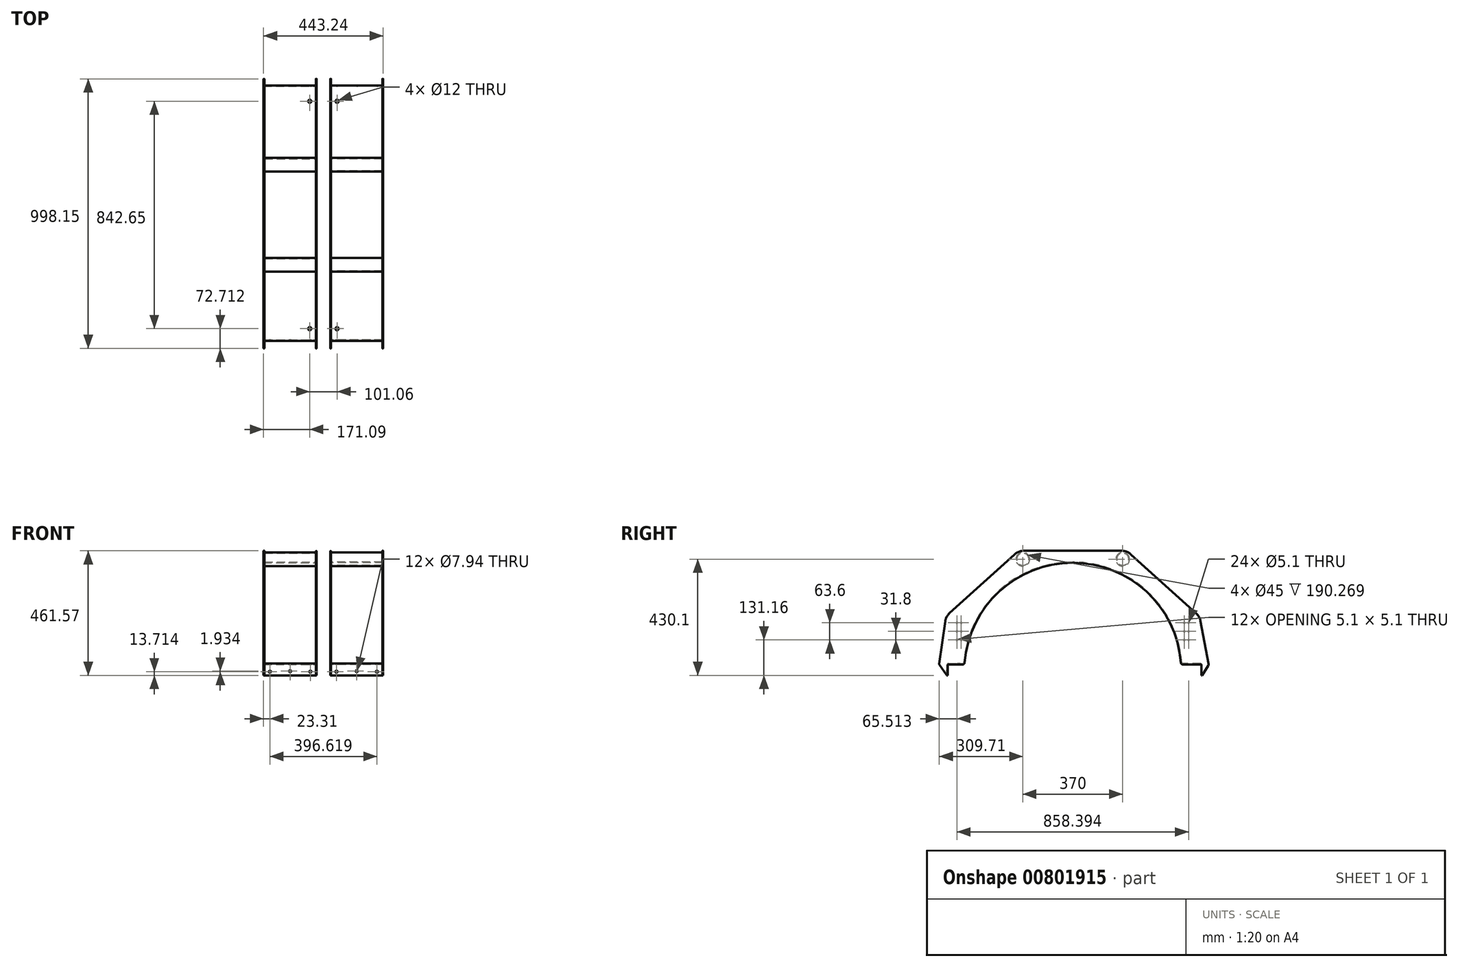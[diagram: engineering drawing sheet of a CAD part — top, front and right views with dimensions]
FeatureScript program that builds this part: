
annotation { "Feature Type Name" : "Feature", "Feature Type Description" : "" }
export const myFeature = defineFeature(function(context is Context, id is Id, definition is map)
    precondition{}
    {
        {
            var Q0;
            Q0=qCreatedBy(makeId("Right.planeOp"),FACE);
            var sketch = newSketch(context, id + "F0", { "sketchPlane" : qUnion([Q0])});
            skArc(sketch, "E0", {"start": v(-400.78, 31.26) * mm, "mid": v(0, 402) * mm, "end": v(400.78, 31.26) * mm});
            skLineSegment(sketch, "E1", {"start": v(-456.53, 215.37) * mm, "end": v(-216.59, 432.1) * mm});
            skLineSegment(sketch, "E2", {"start": v(457.5, 214.5) * mm, "end": v(216.59, 432.1) * mm});
            skLineSegment(sketch, "E3", {"start": v(183.07, 445) * mm, "end": v(-183.07, 445) * mm});
            skLineSegment(sketch, "E4", {"start": v(407.11, 25.4) * mm, "end": v(473.02, 25.4) * mm});
            skLineSegment(sketch, "E5", {"start": v(-460.32, 25.4) * mm, "end": v(-407.11, 25.4) * mm});
            skPoint(sketch, "E6.visualSharp", {"position": v(202.3, 445) * mm});
            skPoint(sketch, "E7.visualSharp", {"position": v(-401.2, 25.4) * mm});
            skArc(sketch, "E7.filletArc", {"start": v(-407.11, 25.4) * mm, "mid": v(-402.8, 27.09) * mm, "end": v(-400.78, 31.26) * mm});
            skPoint(sketch, "E8.visualSharp", {"position": v(401.2, 25.4) * mm});
            skArc(sketch, "E8.filletArc", {"start": v(400.78, 31.26) * mm, "mid": v(402.8, 27.09) * mm, "end": v(407.11, 25.4) * mm});
            skPoint(sketch, "E9.endSnap0", {"position": v(0, 402) * mm});
            skPoint(sketch, "E10", {"position": v(0, 445) * mm});
            skLineSegment(sketch, "E11", {"start": v(-472.53, 185.23) * mm, "end": v(-494.65, 27.9) * mm});
            skLineSegment(sketch, "E12", {"start": v(-493.54, 23.34) * mm, "end": v(-466.3, -15.1) * mm});
            skLineSegment(sketch, "E13", {"start": v(-463.5, -15.1) * mm, "end": v(-463.5, 22.22) * mm});
            skPoint(sketch, "E14.visualSharp", {"position": v(-470, 203.2) * mm});
            skArc(sketch, "E14.filletArc", {"start": v(-456.53, 215.37) * mm, "mid": v(-467.18, 201.7) * mm, "end": v(-472.53, 185.23) * mm});
            skPoint(sketch, "E15.visualSharp", {"position": v(-495, 25.4) * mm});
            skArc(sketch, "E15.filletArc", {"start": v(-494.65, 27.9) * mm, "mid": v(-494.53, 25.51) * mm, "end": v(-493.54, 23.34) * mm});
            skPoint(sketch, "E16.visualSharp", {"position": v(-463.5, 25.4) * mm});
            skArc(sketch, "E16.filletArc", {"start": v(-460.32, 25.4) * mm, "mid": v(-462.57, 24.47) * mm, "end": v(-463.5, 22.22) * mm});
            skLineSegment(sketch, "E17", {"start": v(476.2, 22.22) * mm, "end": v(476.2, -15.1) * mm});
            skPoint(sketch, "E18", {"position": v(505, 25.4) * mm});
            skLineSegment(sketch, "E19", {"start": v(479.37, -15.1) * mm, "end": v(502.46, 21.38) * mm});
            skLineSegment(sketch, "E20", {"start": v(503.33, 25.95) * mm, "end": v(473.12, 186.63) * mm});
            skPoint(sketch, "E21.visualSharp", {"position": v(470, 203.2) * mm});
            skArc(sketch, "E21.filletArc", {"start": v(473.12, 186.63) * mm, "mid": v(467.59, 201.85) * mm, "end": v(457.5, 214.5) * mm});
            skArc(sketch, "E22.filletArc", {"start": v(502.46, 21.38) * mm, "mid": v(503.33, 23.59) * mm, "end": v(503.33, 25.95) * mm});
            skLineSegment(sketch, "E23", {"start": v(476.2, -15.1) * mm, "end": v(479.37, -15.1) * mm});
            skLineSegment(sketch, "E24", {"start": v(-466.3, -15.1) * mm, "end": v(-463.5, -15.1) * mm});
            skPoint(sketch, "E25.visualSharp", {"position": v(476.2, 25.4) * mm});
            skArc(sketch, "E25.filletArc", {"start": v(476.2, 22.22) * mm, "mid": v(475.27, 24.47) * mm, "end": v(473.02, 25.4) * mm});
            skPoint(sketch, "E26", {"position": v(-429.2, 116.06) * mm});
            skPoint(sketch, "E27", {"position": v(-413.2, 116.06) * mm});
            skPoint(sketch, "E28", {"position": v(-413.2, 147.86) * mm});
            skPoint(sketch, "E29", {"position": v(-429.2, 147.86) * mm});
            skPoint(sketch, "E30", {"position": v(-429.2, 179.66) * mm});
            skPoint(sketch, "E31", {"position": v(-413.2, 179.66) * mm});
            skPoint(sketch, "E32", {"position": v(413.2, 179.66) * mm});
            skPoint(sketch, "E33", {"position": v(429.2, 179.66) * mm});
            skPoint(sketch, "E34", {"position": v(429.2, 147.86) * mm});
            skPoint(sketch, "E35", {"position": v(413.2, 147.86) * mm});
            skPoint(sketch, "E36", {"position": v(413.2, 116.06) * mm});
            skPoint(sketch, "E37", {"position": v(429.2, 116.06) * mm});
            skLineSegment(sketch, "E38.bottom", {"start": v(413.2, 179.66) * mm, "end": v(429.2, 179.66) * mm, "construction": true});
            skLineSegment(sketch, "E38.top", {"start": v(413.2, 116.06) * mm, "end": v(429.2, 116.06) * mm, "construction": true});
            skLineSegment(sketch, "E38.left", {"start": v(413.2, 179.66) * mm, "end": v(413.2, 116.06) * mm, "construction": true});
            skLineSegment(sketch, "E38.right", {"start": v(429.2, 179.66) * mm, "end": v(429.2, 116.06) * mm, "construction": true});
            skLineSegment(sketch, "E39", {"start": v(0, 0) * mm, "end": v(0, 524.96) * mm, "construction": true});
            skPoint(sketch, "E40.visualSharp", {"position": v(-202.31, 445) * mm});
            skArc(sketch, "E40.filletArc", {"start": v(-183.07, 445) * mm, "mid": v(-201.03, 441.66) * mm, "end": v(-216.59, 432.1) * mm});
            skPoint(sketch, "E41.newPointB", {"position": v(202.31, 445) * mm});
            skArc(sketch, "E41.filletArc", {"start": v(216.59, 432.1) * mm, "mid": v(201.03, 441.66) * mm, "end": v(183.07, 445) * mm});
            skSolve(sketch);
        }
        {
            var Q0;
            Q0=qSketchRegion(id+"F0",true);
            extrude(context, id + "F1", {"entities" : qUnion([Q0]), "depth" : 3.17 * mm});
        }
        {
            var Q0;
            Q0=makeQuery(id+"F1.opExtrude","CAP_FACE",FACE,{"disambiguationData":[OSD([sQuery(id+"F0.wireOp",EDGE,"E0"),sQuery(id+"F0.wireOp",EDGE,"E9loCTzL-wOmK-y6Et-Pe2N-kgU0UY5jq1ZF"),sQuery(id+"F0.wireOp",EDGE,"E1"),sQuery(id+"F0.wireOp",EDGE,"s9JNnq10-T5jz-dtBx-Jel8-L66kQnyxZmdq"),sQuery(id+"F0.wireOp",EDGE,"E2"),sQuery(id+"F0.wireOp",EDGE,"E3"),sQuery(id+"F0.wireOp",EDGE,"E4"),sQuery(id+"F0.wireOp",EDGE,"E5"),sQuery(id+"F0.wireOp",EDGE,"86fa77fb-b35d-4607-8103-cc9440c46565.filletArc"),sQuery(id+"F0.wireOp",EDGE,"56854ff8-0e41-4e1b-8477-ec3efaea42f3.filletArc"),sQuery(id+"F0.wireOp",EDGE,"E6.filletArc"),sQuery(id+"F0.wireOp",EDGE,"a73865e9-f12d-4e8d-86f3-43cc75951e77.filletArc")])],"isStart":false});
            var sketch = newSketch(context, id + "F2", { "sketchPlane" : qUnion([Q0])});
            skArc(sketch, "E42", {"start": v(-400.78, 31.26) * mm, "mid": v(0, 402) * mm, "end": v(400.78, 31.26) * mm});
            skArc(sketch, "E43", {"start": v(-403.95, 31.5) * mm, "mid": v(0, 405.18) * mm, "end": v(403.95, 31.5) * mm});
            skLineSegment(sketch, "E44", {"start": v(-460.32, 28.57) * mm, "end": v(-407.11, 28.57) * mm});
            skLineSegment(sketch, "E45", {"start": v(-460.32, 25.4) * mm, "end": v(-407.11, 25.4) * mm});
            skArc(sketch, "E46.filletArc", {"start": v(-407.11, 25.4) * mm, "mid": v(-402.8, 27.09) * mm, "end": v(-400.78, 31.26) * mm});
            skArc(sketch, "E47.filletArc", {"start": v(-407.11, 28.57) * mm, "mid": v(-404.96, 29.42) * mm, "end": v(-403.95, 31.5) * mm});
            skLineSegment(sketch, "E48", {"start": v(473.02, 28.58) * mm, "end": v(407.11, 28.57) * mm});
            skLineSegment(sketch, "E49", {"start": v(473.02, 25.4) * mm, "end": v(407.11, 25.4) * mm});
            skArc(sketch, "E50.filletArc", {"start": v(400.78, 31.26) * mm, "mid": v(402.8, 27.09) * mm, "end": v(407.11, 25.4) * mm});
            skArc(sketch, "E51.filletArc", {"start": v(403.95, 31.5) * mm, "mid": v(404.96, 29.42) * mm, "end": v(407.11, 28.57) * mm});
            skLineSegment(sketch, "E52", {"start": v(-466.67, 22.22) * mm, "end": v(-466.67, -15.1) * mm});
            skLineSegment(sketch, "E53", {"start": v(-463.5, 22.22) * mm, "end": v(-463.5, -15.1) * mm});
            skLineSegment(sketch, "E54", {"start": v(-463.5, -15.1) * mm, "end": v(-466.67, -15.1) * mm});
            skPoint(sketch, "E55.visualSharp", {"position": v(-463.5, 25.4) * mm});
            skArc(sketch, "E55.filletArc", {"start": v(-460.32, 25.4) * mm, "mid": v(-462.57, 24.47) * mm, "end": v(-463.5, 22.22) * mm});
            skPoint(sketch, "E56.visualSharp", {"position": v(-466.67, 28.57) * mm});
            skArc(sketch, "E56.filletArc", {"start": v(-460.32, 28.57) * mm, "mid": v(-464.81, 26.72) * mm, "end": v(-466.67, 22.22) * mm});
            skLineSegment(sketch, "E57", {"start": v(476.2, 22.23) * mm, "end": v(476.2, -15.1) * mm});
            skLineSegment(sketch, "E58", {"start": v(476.2, -15.1) * mm, "end": v(479.37, -15.1) * mm});
            skLineSegment(sketch, "E59", {"start": v(479.37, -15.1) * mm, "end": v(479.37, 22.23) * mm});
            skPoint(sketch, "E60.visualSharp", {"position": v(476.2, 25.4) * mm});
            skArc(sketch, "E60.filletArc", {"start": v(476.2, 22.23) * mm, "mid": v(475.27, 24.47) * mm, "end": v(473.02, 25.4) * mm});
            skPoint(sketch, "E61.visualSharp", {"position": v(479.37, 28.58) * mm});
            skArc(sketch, "E61.filletArc", {"start": v(479.37, 22.23) * mm, "mid": v(477.51, 26.72) * mm, "end": v(473.02, 28.58) * mm});
            skSolve(sketch);
        }
        {
            var Q0;
            Q0=qSketchRegion(id+"F2",true);
            extrude(context, id + "F3", {"entities" : qUnion([Q0]), "operationType" : NewBodyOperationType.ADD, "depth" : 190.27 * mm});
        }
        {
            var Q0;
            Q0=makeQuery(id+"F3.opExtrude","CAP_FACE",FACE,{"disambiguationData":[OSD([sQuery(id+"F2.wireOp",EDGE,"E42"),sQuery(id+"F2.wireOp",EDGE,"E43"),sQuery(id+"F2.wireOp",EDGE,"Qj5uD3Kj-Tnei-hYOQ-ZmSB-v0AgtbXvPEYO"),sQuery(id+"F2.wireOp",EDGE,"4pAmY6wd-Oeoi-wrFi-XpuQ-VInCCUa1Rv9z")])],"isStart":false});
            var sketch = newSketch(context, id + "F4", { "sketchPlane" : qUnion([Q0])});
            skArc(sketch, "E62", {"start": v(-400.78, 31.26) * mm, "mid": v(0, 402) * mm, "end": v(400.78, 31.26) * mm});
            skLineSegment(sketch, "E63", {"start": v(-456.31, 215.56) * mm, "end": v(-215.19, 433.37) * mm});
            skLineSegment(sketch, "E64", {"start": v(457.3, 214.68) * mm, "end": v(215.19, 433.37) * mm});
            skLineSegment(sketch, "E65", {"start": v(181.14, 446.47) * mm, "end": v(-181.14, 446.47) * mm});
            skPoint(sketch, "E66.visualSharp", {"position": v(-200.68, 446.47) * mm});
            skArc(sketch, "E66.filletArc", {"start": v(-181.14, 446.47) * mm, "mid": v(-199.38, 443.08) * mm, "end": v(-215.19, 433.37) * mm});
            skPoint(sketch, "E67.visualSharp", {"position": v(200.68, 446.47) * mm});
            skArc(sketch, "E67.filletArc", {"start": v(215.19, 433.37) * mm, "mid": v(199.38, 443.08) * mm, "end": v(181.14, 446.47) * mm});
            skPoint(sketch, "E68.visualSharp", {"position": v(398.78, 50.8) * mm});
            skLineSegment(sketch, "E69", {"start": v(0, 0) * mm, "end": v(0.42, 473.33) * mm, "construction": true});
            skPoint(sketch, "E69.endSnap0", {"position": v(0.42, 402) * mm});
            skLineSegment(sketch, "E70", {"start": v(-472.57, 184.94) * mm, "end": v(-494.65, 27.9) * mm});
            skArc(sketch, "E71.filletArc", {"start": v(-456.31, 215.56) * mm, "mid": v(-467.13, 201.68) * mm, "end": v(-472.57, 184.94) * mm});
            skLineSegment(sketch, "E72", {"start": v(473.17, 186.37) * mm, "end": v(503.33, 25.95) * mm});
            skArc(sketch, "E73.filletArc", {"start": v(473.17, 186.37) * mm, "mid": v(467.55, 201.83) * mm, "end": v(457.3, 214.68) * mm});
            skLineSegment(sketch, "E74", {"start": v(407.11, 25.4) * mm, "end": v(473.02, 25.4) * mm});
            skPoint(sketch, "E74.endSnap0", {"position": v(440.07, 25.4) * mm});
            skLineSegment(sketch, "E75", {"start": v(476.2, 22.22) * mm, "end": v(476.2, -15.1) * mm});
            skPoint(sketch, "E76.newPointA", {"position": v(481.52, 25.4) * mm});
            skArc(sketch, "E76.filletArc", {"start": v(476.2, 22.22) * mm, "mid": v(475.27, 24.47) * mm, "end": v(473.02, 25.4) * mm});
            skLineSegment(sketch, "E77", {"start": v(-407.11, 25.4) * mm, "end": v(-460.32, 25.4) * mm});
            skArc(sketch, "E78.filletArc", {"start": v(502.46, 21.38) * mm, "mid": v(503.33, 23.59) * mm, "end": v(503.33, 25.95) * mm});
            skLineSegment(sketch, "E79", {"start": v(-463.5, 22.22) * mm, "end": v(-463.5, -14.56) * mm});
            skLineSegment(sketch, "E80", {"start": v(-493.54, 23.34) * mm, "end": v(-466.67, -14.56) * mm});
            skPoint(sketch, "E81.newPointA", {"position": v(-497.1, 28.36) * mm});
            skPoint(sketch, "E81.newPointB", {"position": v(-494.58, 28.36) * mm});
            skArc(sketch, "E81.filletArc", {"start": v(-494.65, 27.9) * mm, "mid": v(-494.53, 25.51) * mm, "end": v(-493.54, 23.34) * mm});
            skArc(sketch, "E82.filletArc", {"start": v(-407.11, 25.4) * mm, "mid": v(-402.8, 27.09) * mm, "end": v(-400.78, 31.26) * mm});
            skArc(sketch, "E83.filletArc", {"start": v(400.78, 31.26) * mm, "mid": v(402.8, 27.09) * mm, "end": v(407.11, 25.4) * mm});
            skArc(sketch, "E84.filletArc", {"start": v(-460.32, 25.4) * mm, "mid": v(-462.57, 24.47) * mm, "end": v(-463.5, 22.22) * mm});
            skLineSegment(sketch, "E85", {"start": v(479.37, -15.1) * mm, "end": v(476.2, -15.1) * mm});
            skLineSegment(sketch, "E86.trimOffspring", {"start": v(479.37, -15.1) * mm, "end": v(502.46, 21.38) * mm});
            skLineSegment(sketch, "E87", {"start": v(-466.67, -14.56) * mm, "end": v(-463.5, -14.56) * mm});
            skSolve(sketch);
        }
        {
            var Q0;
            Q0=qSketchRegion(id+"F4",true);
            extrude(context, id + "F5", {"entities" : qUnion([Q0]), "operationType" : NewBodyOperationType.ADD, "depth" : 3.17 * mm});
        }
        {
            var Q0;
            Q0=makeQuery(id+"F1.opExtrude","CAP_FACE",FACE,{"disambiguationData":[OSD([sQuery(id+"F0.wireOp",EDGE,"E0"),sQuery(id+"F0.wireOp",EDGE,"E9loCTzL-wOmK-y6Et-Pe2N-kgU0UY5jq1ZF"),sQuery(id+"F0.wireOp",EDGE,"E1"),sQuery(id+"F0.wireOp",EDGE,"s9JNnq10-T5jz-dtBx-Jel8-L66kQnyxZmdq"),sQuery(id+"F0.wireOp",EDGE,"E2"),sQuery(id+"F0.wireOp",EDGE,"E3"),sQuery(id+"F0.wireOp",EDGE,"E4"),sQuery(id+"F0.wireOp",EDGE,"E5"),sQuery(id+"F0.wireOp",EDGE,"86fa77fb-b35d-4607-8103-cc9440c46565.filletArc"),sQuery(id+"F0.wireOp",EDGE,"56854ff8-0e41-4e1b-8477-ec3efaea42f3.filletArc"),sQuery(id+"F0.wireOp",EDGE,"E6.filletArc"),sQuery(id+"F0.wireOp",EDGE,"a73865e9-f12d-4e8d-86f3-43cc75951e77.filletArc")])],"isStart":false});
            var sketch = newSketch(context, id + "F6", { "sketchPlane" : qUnion([Q0])});
            skCircle(sketch, "E88", {"center": v(185, 415) * mm, "radius": 25.4 * mm});
            skCircle(sketch, "E89", {"center": v(185, 415) * mm, "radius": 22.5 * mm});
            skCircle(sketch, "E90", {"center": v(-185, 415) * mm, "radius": 25.4 * mm});
            skCircle(sketch, "E91", {"center": v(-185, 415) * mm, "radius": 22.5 * mm});
            skSolve(sketch);
        }
        {
            var Q0;
            Q0=qSketchRegion(id+"F6",true);
            extrude(context, id + "F7", {"entities" : qUnion([Q0]), "operationType" : NewBodyOperationType.ADD, "depth" : 190.27 * mm});
        }
        {
            var Q0;
            Q0=sQuery(id+"F0.wireOp",VERTEX,"E33");
            var Q1;
            Q1=sQuery(id+"F0.wireOp",VERTEX,"E32");
            var Q2;
            Q2=sQuery(id+"F0.wireOp",VERTEX,"E35");
            var Q3;
            Q3=sQuery(id+"F0.wireOp",VERTEX,"E34");
            var Q4;
            Q4=sQuery(id+"F0.wireOp",VERTEX,"E37");
            var Q5;
            Q5=sQuery(id+"F0.wireOp",VERTEX,"E36");
            var Q6;
            Q6=sQuery(id+"F0.wireOp",VERTEX,"E31");
            var Q7;
            Q7=sQuery(id+"F0.wireOp",VERTEX,"E30");
            var Q8;
            Q8=sQuery(id+"F0.wireOp",VERTEX,"E29");
            var Q9;
            Q9=sQuery(id+"F0.wireOp",VERTEX,"E28");
            var Q10;
            Q10=sQuery(id+"F0.wireOp",VERTEX,"E27");
            var Q11;
            Q11=sQuery(id+"F0.wireOp",VERTEX,"E26");
            var Q12;
            Q12=makeQuery(id+"F1.opExtrude","SWEPT_BODY",BODY,{"disambiguationData":[OSD([sQuery(id+"F0.wireOp",EDGE,"E0"),sQuery(id+"F0.wireOp",EDGE,"E1"),sQuery(id+"F0.wireOp",EDGE,"E2"),sQuery(id+"F0.wireOp",EDGE,"E3"),sQuery(id+"F0.wireOp",EDGE,"E4"),sQuery(id+"F0.wireOp",EDGE,"E5"),sQuery(id+"F0.wireOp",EDGE,"56854ff8-0e41-4e1b-8477-ec3efaea42f3.filletArc"),sQuery(id+"F0.wireOp",EDGE,"E6.filletArc"),sQuery(id+"F0.wireOp",EDGE,"E7.filletArc"),sQuery(id+"F0.wireOp",EDGE,"E8.filletArc"),sQuery(id+"F0.wireOp",EDGE,"E11"),sQuery(id+"F0.wireOp",EDGE,"E12"),sQuery(id+"F0.wireOp",EDGE,"E13"),sQuery(id+"F0.wireOp",EDGE,"E14.filletArc"),sQuery(id+"F0.wireOp",EDGE,"E15.filletArc"),sQuery(id+"F0.wireOp",EDGE,"E16.filletArc"),sQuery(id+"F0.wireOp",EDGE,"E17"),sQuery(id+"F0.wireOp",EDGE,"E19"),sQuery(id+"F0.wireOp",EDGE,"E20"),sQuery(id+"F0.wireOp",EDGE,"E21.filletArc"),sQuery(id+"F0.wireOp",EDGE,"E22.filletArc"),sQuery(id+"F0.wireOp",EDGE,"E23"),sQuery(id+"F0.wireOp",EDGE,"E24"),sQuery(id+"F0.wireOp",EDGE,"E25.filletArc")])]});
            hole(context, id + "F8", {"style" : HoleStyle.SIMPLE, "endStyle" : HoleEndStyle.BLIND, "oppositeDirection" : true, "holeDiameter" : 5.1 * mm, "holeDepth" : 17.75 * mm, "isTappedThrough" : true, "tappedDepth" : 10.25 * mm, "tapClearance" : 3, "startFromSketch" : true, "locations" : qUnion([Q0, Q1, Q2, Q3, Q4, Q5, Q6, Q7, Q8, Q9, Q10, Q11]), "scope" : qUnion([Q12])});
        }
        {
            var Q0;
            Q0=qCreatedBy(makeId("Right.planeOp"),FACE);
            cPlane(context, id + "F9", {"entities" : qUnion([Q0]), "cplaneType" : CPlaneType.OFFSET, "offset" : 25 * mm, "oppositeDirection" : true, "width" : 150 * mm, "height" : 150 * mm});
        }
        {
            var Q0;
            Q0=makeQuery(id+"F1.opExtrude","SWEPT_BODY",BODY,{"disambiguationData":[OSD([sQuery(id+"F0.wireOp",EDGE,"E0"),sQuery(id+"F0.wireOp",EDGE,"E1"),sQuery(id+"F0.wireOp",EDGE,"E2"),sQuery(id+"F0.wireOp",EDGE,"E3"),sQuery(id+"F0.wireOp",EDGE,"E4"),sQuery(id+"F0.wireOp",EDGE,"E5"),sQuery(id+"F0.wireOp",EDGE,"56854ff8-0e41-4e1b-8477-ec3efaea42f3.filletArc"),sQuery(id+"F0.wireOp",EDGE,"E6.filletArc"),sQuery(id+"F0.wireOp",EDGE,"E7.filletArc"),sQuery(id+"F0.wireOp",EDGE,"E8.filletArc"),sQuery(id+"F0.wireOp",EDGE,"E11"),sQuery(id+"F0.wireOp",EDGE,"E12"),sQuery(id+"F0.wireOp",EDGE,"E13"),sQuery(id+"F0.wireOp",EDGE,"E14.filletArc"),sQuery(id+"F0.wireOp",EDGE,"E15.filletArc"),sQuery(id+"F0.wireOp",EDGE,"E16.filletArc"),sQuery(id+"F0.wireOp",EDGE,"E17"),sQuery(id+"F0.wireOp",EDGE,"E19"),sQuery(id+"F0.wireOp",EDGE,"E20"),sQuery(id+"F0.wireOp",EDGE,"E21.filletArc"),sQuery(id+"F0.wireOp",EDGE,"E22.filletArc"),sQuery(id+"F0.wireOp",EDGE,"E23"),sQuery(id+"F0.wireOp",EDGE,"E24"),sQuery(id+"F0.wireOp",EDGE,"E25.filletArc")])]});
            var Q1;
            Q1=qCreatedBy(id+"F9.planeOp",FACE);
            mirror(context, id + "F10", {"entities" : qUnion([Q0]), "mirrorPlane" : qUnion([Q1])});
        }
        {
            var Q0;
            Q0=makeQuery(id+"F10.opPattern","COPY",BODY,{"derivedFrom":makeQuery(id+"F1.opExtrude","SWEPT_BODY",BODY,{"disambiguationData":[OSD([sQuery(id+"F0.wireOp",EDGE,"E0"),sQuery(id+"F0.wireOp",EDGE,"E1"),sQuery(id+"F0.wireOp",EDGE,"E2"),sQuery(id+"F0.wireOp",EDGE,"E3"),sQuery(id+"F0.wireOp",EDGE,"E4"),sQuery(id+"F0.wireOp",EDGE,"E5"),sQuery(id+"F0.wireOp",EDGE,"56854ff8-0e41-4e1b-8477-ec3efaea42f3.filletArc"),sQuery(id+"F0.wireOp",EDGE,"E6.filletArc"),sQuery(id+"F0.wireOp",EDGE,"E7.filletArc"),sQuery(id+"F0.wireOp",EDGE,"E8.filletArc"),sQuery(id+"F0.wireOp",EDGE,"E11"),sQuery(id+"F0.wireOp",EDGE,"E12"),sQuery(id+"F0.wireOp",EDGE,"E13"),sQuery(id+"F0.wireOp",EDGE,"E14.filletArc"),sQuery(id+"F0.wireOp",EDGE,"E15.filletArc"),sQuery(id+"F0.wireOp",EDGE,"E16.filletArc"),sQuery(id+"F0.wireOp",EDGE,"E17"),sQuery(id+"F0.wireOp",EDGE,"E19"),sQuery(id+"F0.wireOp",EDGE,"E20"),sQuery(id+"F0.wireOp",EDGE,"E21.filletArc"),sQuery(id+"F0.wireOp",EDGE,"E22.filletArc"),sQuery(id+"F0.wireOp",EDGE,"E23"),sQuery(id+"F0.wireOp",EDGE,"E24"),sQuery(id+"F0.wireOp",EDGE,"E25.filletArc")])]}),"instanceName":"1"});
            deleteBodies(context, id + "F11", {"entities" : qUnion([Q0])});
        }
        {
            var Q0;
            Q0=makeQuery(id+"F3.opExtrude","SWEPT_FACE",FACE,{"disambiguationData":[OSD([sQuery(id+"F2.wireOp",EDGE,"E52")])]});
            var sketch = newSketch(context, id + "F12", { "sketchPlane" : qUnion([Q0])});
            skLineSegment(sketch, "E92", {"start": v(-18.58, -1.39) * mm, "end": v(188.45, -1.39) * mm, "construction": true});
            skLineSegment(sketch, "E93", {"start": v(23.3, -19.94) * mm, "end": v(23.3, 12.68) * mm, "construction": true});
            skLineSegment(sketch, "E94", {"start": v(173.3, -20.85) * mm, "end": v(173.3, 12.98) * mm, "construction": true});
            skPoint(sketch, "E95", {"position": v(23.3, -1.39) * mm});
            skPoint(sketch, "E96", {"position": v(98.3, -1.39) * mm});
            skPoint(sketch, "E97", {"position": v(173.3, -1.39) * mm});
            skPoint(sketch, "E98", {"position": v(98.3, 0.55) * mm});
            skSolve(sketch);
        }
        {
            var Q0;
            Q0=sQuery(id+"F12.wireOp",VERTEX,"E95");
            var Q1;
            Q1=sQuery(id+"F12.wireOp",VERTEX,"E97");
            var Q2;
            Q2=sQuery(id+"F12.wireOp",VERTEX,"E98");
            var Q3;
            Q3=makeQuery(id+"F1.opExtrude","SWEPT_BODY",BODY,{"disambiguationData":[OSD([sQuery(id+"F0.wireOp",EDGE,"E0"),sQuery(id+"F0.wireOp",EDGE,"E1"),sQuery(id+"F0.wireOp",EDGE,"E2"),sQuery(id+"F0.wireOp",EDGE,"E3"),sQuery(id+"F0.wireOp",EDGE,"E4"),sQuery(id+"F0.wireOp",EDGE,"E5"),sQuery(id+"F0.wireOp",EDGE,"56854ff8-0e41-4e1b-8477-ec3efaea42f3.filletArc"),sQuery(id+"F0.wireOp",EDGE,"E6.filletArc"),sQuery(id+"F0.wireOp",EDGE,"E7.filletArc"),sQuery(id+"F0.wireOp",EDGE,"E8.filletArc"),sQuery(id+"F0.wireOp",EDGE,"E11"),sQuery(id+"F0.wireOp",EDGE,"E12"),sQuery(id+"F0.wireOp",EDGE,"E13"),sQuery(id+"F0.wireOp",EDGE,"E14.filletArc"),sQuery(id+"F0.wireOp",EDGE,"E15.filletArc"),sQuery(id+"F0.wireOp",EDGE,"E16.filletArc"),sQuery(id+"F0.wireOp",EDGE,"E17"),sQuery(id+"F0.wireOp",EDGE,"E19"),sQuery(id+"F0.wireOp",EDGE,"E20"),sQuery(id+"F0.wireOp",EDGE,"E21.filletArc"),sQuery(id+"F0.wireOp",EDGE,"E22.filletArc"),sQuery(id+"F0.wireOp",EDGE,"E23"),sQuery(id+"F0.wireOp",EDGE,"E24"),sQuery(id+"F0.wireOp",EDGE,"E25.filletArc")])]});
            hole(context, id + "F13", {"style" : HoleStyle.SIMPLE, "endStyle" : HoleEndStyle.THROUGH, "holeDiameter" : 7.94 * mm, "isTappedThrough" : true, "tappedDepth" : 10.25 * mm, "tapClearance" : 3, "startFromSketch" : true, "locations" : qUnion([Q0, Q1, Q2]), "scope" : qUnion([Q3]), "majorDiameter" : 5 * mm});
        }
        {
            var Q0;
            Q0=makeQuery(id+"F1.opExtrude","SWEPT_BODY",BODY,{"disambiguationData":[OSD([sQuery(id+"F0.wireOp",EDGE,"E0"),sQuery(id+"F0.wireOp",EDGE,"E1"),sQuery(id+"F0.wireOp",EDGE,"E2"),sQuery(id+"F0.wireOp",EDGE,"E3"),sQuery(id+"F0.wireOp",EDGE,"E4"),sQuery(id+"F0.wireOp",EDGE,"E5"),sQuery(id+"F0.wireOp",EDGE,"56854ff8-0e41-4e1b-8477-ec3efaea42f3.filletArc"),sQuery(id+"F0.wireOp",EDGE,"E6.filletArc"),sQuery(id+"F0.wireOp",EDGE,"E7.filletArc"),sQuery(id+"F0.wireOp",EDGE,"E8.filletArc"),sQuery(id+"F0.wireOp",EDGE,"E11"),sQuery(id+"F0.wireOp",EDGE,"E12"),sQuery(id+"F0.wireOp",EDGE,"E13"),sQuery(id+"F0.wireOp",EDGE,"E14.filletArc"),sQuery(id+"F0.wireOp",EDGE,"E15.filletArc"),sQuery(id+"F0.wireOp",EDGE,"E16.filletArc"),sQuery(id+"F0.wireOp",EDGE,"E17"),sQuery(id+"F0.wireOp",EDGE,"E19"),sQuery(id+"F0.wireOp",EDGE,"E20"),sQuery(id+"F0.wireOp",EDGE,"E21.filletArc"),sQuery(id+"F0.wireOp",EDGE,"E22.filletArc"),sQuery(id+"F0.wireOp",EDGE,"E23"),sQuery(id+"F0.wireOp",EDGE,"E24"),sQuery(id+"F0.wireOp",EDGE,"E25.filletArc")])]});
            var Q1;
            Q1=qCreatedBy(id+"F9.planeOp",FACE);
            mirror(context, id + "F14", {"entities" : qUnion([Q0]), "mirrorPlane" : qUnion([Q1])});
        }
        {
            var Q0;
            Q0=makeQuery(id+"F3.opExtrude","SWEPT_FACE",FACE,{"disambiguationData":[OSD([sQuery(id+"F2.wireOp",EDGE,"E44")])]});
            var sketch = newSketch(context, id + "F15", { "sketchPlane" : qUnion([Q0])});
            skCircle(sketch, "E99", {"center": v(25.53, -422) * mm, "radius": 6 * mm});
            skSolve(sketch);
        }
        {
            var Q0;
            Q0=qSketchRegion(id+"F15",true);
            extrude(context, id + "F16", {"entities" : qUnion([Q0]), "operationType" : NewBodyOperationType.REMOVE, "oppositeDirection" : true, "depth" : 25 * mm});
        }
        {
            var Q0;
            Q0=makeQuery(id+"F3.opExtrude","SWEPT_FACE",FACE,{"disambiguationData":[OSD([sQuery(id+"F2.wireOp",EDGE,"E48")])]});
            var sketch = newSketch(context, id + "F17", { "sketchPlane" : qUnion([Q0])});
            skCircle(sketch, "E100", {"center": v(25.53, 420.65) * mm, "radius": 6 * mm});
            skSolve(sketch);
        }
        {
            var Q0;
            Q0=qSketchRegion(id+"F17",true);
            extrude(context, id + "F18", {"entities" : qUnion([Q0]), "operationType" : NewBodyOperationType.REMOVE, "oppositeDirection" : true, "depth" : 25 * mm});
        }
        {
            var Q0;
            Q0=makeQuery(id+"F14.opPattern","COPY",BODY,{"derivedFrom":makeQuery(id+"F1.opExtrude","SWEPT_BODY",BODY,{"disambiguationData":[OSD([sQuery(id+"F0.wireOp",EDGE,"E0"),sQuery(id+"F0.wireOp",EDGE,"E1"),sQuery(id+"F0.wireOp",EDGE,"E2"),sQuery(id+"F0.wireOp",EDGE,"E3"),sQuery(id+"F0.wireOp",EDGE,"E4"),sQuery(id+"F0.wireOp",EDGE,"E5"),sQuery(id+"F0.wireOp",EDGE,"56854ff8-0e41-4e1b-8477-ec3efaea42f3.filletArc"),sQuery(id+"F0.wireOp",EDGE,"E6.filletArc"),sQuery(id+"F0.wireOp",EDGE,"E7.filletArc"),sQuery(id+"F0.wireOp",EDGE,"E8.filletArc"),sQuery(id+"F0.wireOp",EDGE,"E11"),sQuery(id+"F0.wireOp",EDGE,"E12"),sQuery(id+"F0.wireOp",EDGE,"E13"),sQuery(id+"F0.wireOp",EDGE,"E14.filletArc"),sQuery(id+"F0.wireOp",EDGE,"E15.filletArc"),sQuery(id+"F0.wireOp",EDGE,"E16.filletArc"),sQuery(id+"F0.wireOp",EDGE,"E17"),sQuery(id+"F0.wireOp",EDGE,"E19"),sQuery(id+"F0.wireOp",EDGE,"E20"),sQuery(id+"F0.wireOp",EDGE,"E21.filletArc"),sQuery(id+"F0.wireOp",EDGE,"E22.filletArc"),sQuery(id+"F0.wireOp",EDGE,"E23"),sQuery(id+"F0.wireOp",EDGE,"E24"),sQuery(id+"F0.wireOp",EDGE,"E25.filletArc")])]}),"instanceName":"1"});
            deleteBodies(context, id + "F19", {"entities" : qUnion([Q0])});
        }
        {
            var Q0;
            Q0=makeQuery(id+"F1.opExtrude","SWEPT_BODY",BODY,{"disambiguationData":[OSD([sQuery(id+"F0.wireOp",EDGE,"E0"),sQuery(id+"F0.wireOp",EDGE,"E1"),sQuery(id+"F0.wireOp",EDGE,"E2"),sQuery(id+"F0.wireOp",EDGE,"E3"),sQuery(id+"F0.wireOp",EDGE,"E4"),sQuery(id+"F0.wireOp",EDGE,"E5"),sQuery(id+"F0.wireOp",EDGE,"56854ff8-0e41-4e1b-8477-ec3efaea42f3.filletArc"),sQuery(id+"F0.wireOp",EDGE,"E6.filletArc"),sQuery(id+"F0.wireOp",EDGE,"E7.filletArc"),sQuery(id+"F0.wireOp",EDGE,"E8.filletArc"),sQuery(id+"F0.wireOp",EDGE,"E11"),sQuery(id+"F0.wireOp",EDGE,"E12"),sQuery(id+"F0.wireOp",EDGE,"E13"),sQuery(id+"F0.wireOp",EDGE,"E14.filletArc"),sQuery(id+"F0.wireOp",EDGE,"E15.filletArc"),sQuery(id+"F0.wireOp",EDGE,"E16.filletArc"),sQuery(id+"F0.wireOp",EDGE,"E17"),sQuery(id+"F0.wireOp",EDGE,"E19"),sQuery(id+"F0.wireOp",EDGE,"E20"),sQuery(id+"F0.wireOp",EDGE,"E21.filletArc"),sQuery(id+"F0.wireOp",EDGE,"E22.filletArc"),sQuery(id+"F0.wireOp",EDGE,"E23"),sQuery(id+"F0.wireOp",EDGE,"E24"),sQuery(id+"F0.wireOp",EDGE,"E25.filletArc")])]});
            var Q1;
            Q1=qCreatedBy(id+"F9.planeOp",FACE);
            mirror(context, id + "F20", {"entities" : qUnion([Q0]), "mirrorPlane" : qUnion([Q1])});
        }
    });
